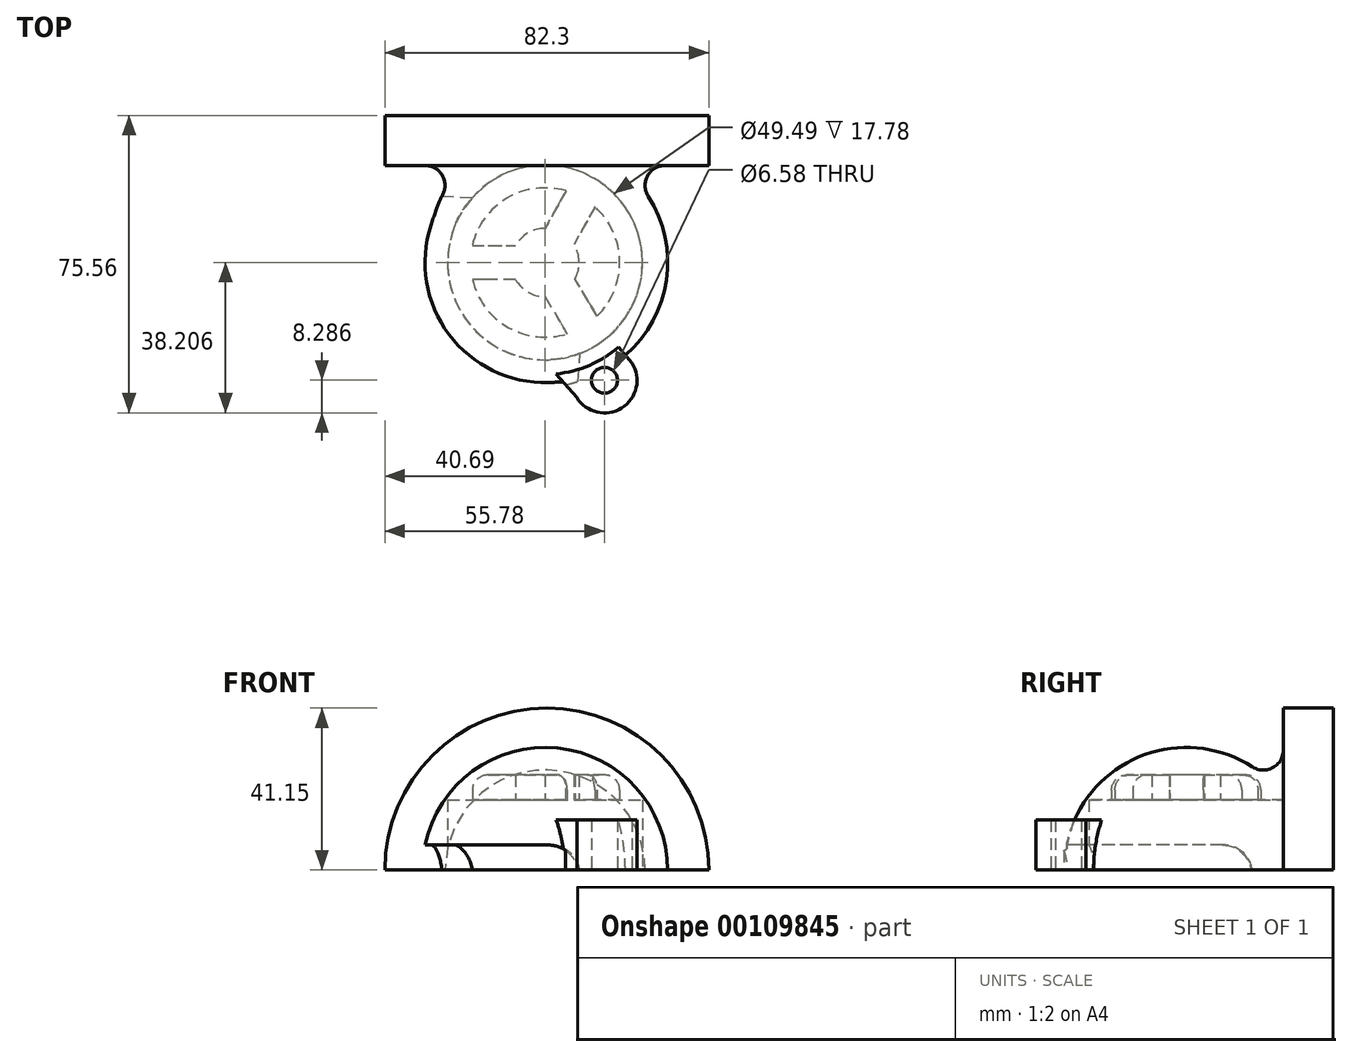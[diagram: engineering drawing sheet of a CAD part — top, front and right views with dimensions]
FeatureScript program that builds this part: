
annotation { "Feature Type Name" : "Feature", "Feature Type Description" : "" }
export const myFeature = defineFeature(function(context is Context, id is Id, definition is map)
    precondition{}
    {
        {
            var Q0;
            Q0=qCreatedBy(makeId("Front.planeOp"),FACE);
            var sketch = newSketch(context, id + "F0", { "sketchPlane" : qUnion([Q0])});
            skArc(sketch, "E0", {"start": v(41.6, 0) * mm, "mid": v(0.46, 41.15) * mm, "end": v(-40.7, 0) * mm});
            skLineSegment(sketch, "E1", {"start": v(-40.7, 0) * mm, "end": v(41.6, 0) * mm});
            skSolve(sketch);
        }
        {
            var Q0;
            Q0 = qSketchRegion(id + "F0", true);
            extrude(context, id + "F1", {"entities" : qUnion([Q0]), "oppositeDirection" : true, "depth" : 12.7 * mm});
        }
        {
            var Q0;
            Q0=qCreatedBy(makeId("Top.planeOp"),FACE);
            var sketch = newSketch(context, id + "F2", { "sketchPlane" : qUnion([Q0])});
            skCircle(sketch, "E2", {"center": v(0, -24.65) * mm, "radius": 31.14 * mm});
            skLineSegment(sketch, "E3", {"start": v(0, -55.8) * mm, "end": v(0, 0) * mm});
            skLineSegment(sketch, "E4", {"start": v(0, -67.73) * mm, "end": v(0, 47.75) * mm, "construction": true});
            skLineSegment(sketch, "E5", {"start": v(0, -55.8) * mm, "end": v(0, 6.5) * mm});
            skSolve(sketch);
        }
        {
            var Q0;
            {var subQ0=sQuery(id+"F2.wireOp",EDGE,"E5");var subQ4=makeQuery(id+"F2.imprint","IMPRINT",VERTEX,{"derivedFrom":subQ0});Q0=makeQuery(id+"F2.imprint","IMPRINT",FACE,{"disambiguationData":[TD([[makeQuery(id+"F2.imprint","IMPRINT",EDGE,{"disambiguationData":[TD([[subQ4,1.0]])],"derivedFrom":subQ0}),-1.0]])]});}
            var Q1;
            Q1=sQuery(id+"F2.wireOp",EDGE,"E4");
            revolve(context, id + "F3", {"operationType" : NewBodyOperationType.ADD, "entities" : qUnion([Q0]), "axis" : qUnion([Q1]), "revolveType" : RevolveType.ONE_DIRECTION, "oppositeDirection" : true, "angle" : 180 * degree});
        }
        {
            var Q0;
            Q0=makeQuery(id+"F3.boolean.opBoolean","INTERSECT",EDGE,{"derivedFrom":[makeQuery(id+"F1.opExtrude","CAP_FACE",FACE,{"disambiguationData":[OSD([sQuery(id+"F0.wireOp",EDGE,"E0"),sQuery(id+"F0.wireOp",EDGE,"E1")])],"isStart":true}),makeQuery(id+"F3.opRevolve","SWEPT_FACE",FACE,{"disambiguationData":[OSD([sQuery(id+"F2.wireOp",EDGE,"E2")])]})]});
            fillet(context, id + "F4", {"entities" : qUnion([Q0]), "radius" : 5.08 * mm, "tangentPropagation" : true, "allowEdgeOverflow" : false});
        }
        {
            var Q0;
            Q0=makeQuery(id+"F3.boolean.opBoolean","MERGE",FACE,{"derivedFrom":[makeQuery(id+"F1.opExtrude","SWEPT_FACE",FACE,{"disambiguationData":[OSD([sQuery(id+"F0.wireOp",EDGE,"E1")])]}),makeQuery(id+"F3.opRevolve","CAP_FACE",FACE,{"disambiguationData":[OSD([sQuery(id+"F2.wireOp",EDGE,"E2"),sQuery(id+"F2.wireOp",EDGE,"E5")])],"isStart":true})]});
            var sketch = newSketch(context, id + "F5", { "sketchPlane" : qUnion([Q0])});
            skCircle(sketch, "E6", {"center": v(0, 24.65) * mm, "radius": 24.75 * mm});
            skSolve(sketch);
        }
        {
            var Q0;
            Q0 = qSketchRegion(id + "F5", true);
            extrude(context, id + "F6", {"entities" : qUnion([Q0]), "operationType" : NewBodyOperationType.REMOVE, "oppositeDirection" : true, "depth" : 17.78 * mm});
        }
        {
            var Q0;
            Q0=makeQuery(id+"F6.boolean.opBoolean","COPY",FACE,{"derivedFrom":makeQuery(id+"F6.opExtrude","CAP_FACE",FACE,{"disambiguationData":[OSD([sQuery(id+"F5.wireOp",EDGE,"E6")])],"isStart":false})});
            var sketch = newSketch(context, id + "F7", { "sketchPlane" : qUnion([Q0])});
            skCircle(sketch, "E7", {"center": v(0, 24.65) * mm, "radius": 18.97 * mm});
            skCircle(sketch, "E8", {"center": v(0, 24.65) * mm, "radius": 8.68 * mm});
            skLineSegment(sketch, "E9", {"start": v(-7.53, 28.97) * mm, "end": v(-18.48, 28.97) * mm});
            skLineSegment(sketch, "E10", {"start": v(-18.48, 28.97) * mm, "end": v(-18.48, 20.34) * mm});
            skLineSegment(sketch, "E11", {"start": v(-18.48, 20.34) * mm, "end": v(-7.53, 20.34) * mm});
            skLineSegment(sketch, "E12", {"start": v(-7.53, 28.97) * mm, "end": v(-7.53, 20.34) * mm});
            skLineSegment(sketch, "E13", {"start": v(0, 33.33) * mm, "end": v(5.61, 42.78) * mm});
            skLineSegment(sketch, "E14", {"start": v(5.33, 6.44) * mm, "end": v(0, 15.98) * mm});
            skLineSegment(sketch, "E15", {"start": v(5.22, 6.41) * mm, "end": v(12.67, 10.53) * mm});
            skLineSegment(sketch, "E16", {"start": v(12.67, 10.53) * mm, "end": v(7.35, 20.04) * mm});
            skLineSegment(sketch, "E17", {"start": v(7.35, 20.04) * mm, "end": v(0, 15.98) * mm});
            skLineSegment(sketch, "E18", {"start": v(5.61, 42.78) * mm, "end": v(13.23, 38.25) * mm});
            skLineSegment(sketch, "E19", {"start": v(13.23, 38.25) * mm, "end": v(7.62, 28.8) * mm});
            skLineSegment(sketch, "E20", {"start": v(7.62, 28.8) * mm, "end": v(0, 33.33) * mm});
            skSolve(sketch);
        }
        {
            var Q0;
            {var subQ0=sQuery(id+"F7.wireOp",EDGE,"E9");Q0=makeQuery(id+"F7.imprint","IMPRINT",FACE,{"disambiguationData":[TD([[makeQuery(id+"F7.imprint","IMPRINT",EDGE,{"derivedFrom":subQ0}),-1.0]])]});}
            var Q1;
            {var subQ0=sQuery(id+"F7.wireOp",EDGE,"E16");Q1=makeQuery(id+"F7.imprint","IMPRINT",FACE,{"disambiguationData":[TD([[makeQuery(id+"F7.imprint","IMPRINT",EDGE,{"derivedFrom":subQ0}),-1.0]])]});}
            var Q2;
            {var subQ0=sQuery(id+"F7.wireOp",EDGE,"E11");Q2=makeQuery(id+"F7.imprint","IMPRINT",FACE,{"disambiguationData":[TD([[makeQuery(id+"F7.imprint","IMPRINT",EDGE,{"derivedFrom":subQ0}),-1.0]])]});}
            extrude(context, id + "F8", {"entities" : qUnion([Q0, Q1, Q2]), "operationType" : NewBodyOperationType.REMOVE, "oppositeDirection" : true, "depth" : 6.35 * mm});
        }
        {
            var Q0;
            Q0=qCreatedBy(makeId("Top.planeOp"),FACE);
            var sketch = newSketch(context, id + "F9", { "sketchPlane" : qUnion([Q0])});
            skLineSegment(sketch, "E21", {"start": v(16.9, -44.18) * mm, "end": v(2.16, -52.16) * mm});
            skArc(sketch, "E22", {"start": v(8.07, -58.97) * mm, "mid": v(19.49, -61.6) * mm, "end": v(22.11, -50.18) * mm});
            skLineSegment(sketch, "E23", {"start": v(22.11, -50.18) * mm, "end": v(16.9, -44.18) * mm});
            skLineSegment(sketch, "E24", {"start": v(8.07, -58.97) * mm, "end": v(2.16, -52.16) * mm});
            skSolve(sketch);
        }
        {
            var Q0;
            Q0 = qSketchRegion(id + "F9", true);
            extrude(context, id + "F10", {"entities" : qUnion([Q0]), "operationType" : NewBodyOperationType.ADD, "depth" : 12.7 * mm});
        }
        {
            var Q0;
            Q0=makeQuery(id+"F10.boolean.opBoolean","MERGE",FACE,{"derivedFrom":[makeQuery(id+"F3.boolean.opBoolean","MERGE",FACE,{"derivedFrom":[makeQuery(id+"F1.opExtrude","SWEPT_FACE",FACE,{"disambiguationData":[OSD([sQuery(id+"F0.wireOp",EDGE,"E1")])]}),makeQuery(id+"F3.opRevolve","CAP_FACE",FACE,{"disambiguationData":[OSD([sQuery(id+"F2.wireOp",EDGE,"E2"),sQuery(id+"F2.wireOp",EDGE,"E5")])],"isStart":true})]}),makeQuery(id+"F10.opExtrude","CAP_FACE",FACE,{"disambiguationData":[OSD([sQuery(id+"F9.wireOp",EDGE,"E21"),sQuery(id+"F9.wireOp",EDGE,"E22"),sQuery(id+"F9.wireOp",EDGE,"E23"),sQuery(id+"F9.wireOp",EDGE,"E24")])],"isStart":true})]});
            var sketch = newSketch(context, id + "F11", { "sketchPlane" : qUnion([Q0])});
            skCircle(sketch, "E25", {"center": v(15.09, 54.57) * mm, "radius": 3.29 * mm});
            skSolve(sketch);
        }
        {
            var Q0;
            Q0 = qSketchRegion(id + "F11", true);
            extrude(context, id + "F12", {"entities" : qUnion([Q0]), "operationType" : NewBodyOperationType.REMOVE, "oppositeDirection" : true, "depth" : 50.8 * mm});
        }
        {
            var Q0;
            Q0=qCreatedBy(makeId("Top.planeOp"),FACE);
            var sketch = newSketch(context, id + "F13", { "sketchPlane" : qUnion([Q0])});
            skArc(sketch, "E26", {"start": v(-26.4, -7.8) * mm, "mid": v(-26.22, -44.06) * mm, "end": v(8.4, -54.85) * mm});
            skArc(sketch, "E27", {"start": v(-16.68, -8.24) * mm, "mid": v(-20.25, -38.17) * mm, "end": v(9.02, -45.34) * mm});
            skLineSegment(sketch, "E28", {"start": v(-26.4, -7.8) * mm, "end": v(-16.68, -8.24) * mm});
            skLineSegment(sketch, "E29", {"start": v(8.4, -54.85) * mm, "end": v(9.02, -45.34) * mm});
            skSolve(sketch);
        }
        {
            var Q0;
            Q0 = qSketchRegion(id + "F13", true);
            extrude(context, id + "F14", {"entities" : qUnion([Q0]), "operationType" : NewBodyOperationType.REMOVE, "depth" : 6.35 * mm});
        }
        {
            var Q0;
            Q0=makeQuery(id+"F14.boolean.opBoolean","COPY",EDGE,{"derivedFrom":makeQuery(id+"F14.opExtrude","CAP_EDGE",EDGE,{"disambiguationData":[OSD([sQuery(id+"F13.wireOp",EDGE,"E29")])],"isStart":false})});
            var Q1;
            Q1=makeQuery(id+"F14.boolean.opBoolean","COPY",EDGE,{"derivedFrom":makeQuery(id+"F14.opExtrude","CAP_EDGE",EDGE,{"disambiguationData":[OSD([sQuery(id+"F13.wireOp",EDGE,"E28")])],"isStart":false})});
            fillet(context, id + "F15", {"entities" : qUnion([Q0, Q1]), "radius" : 7.62 * mm, "tangentPropagation" : true, "allowEdgeOverflow" : false});
        }
        {
            var Q0;
            {var subQ0=sQuery(id+"F7.wireOp",EDGE,"E7");Q0=makeQuery(id+"F8.boolean.opBoolean","COPY",EDGE,{"derivedFrom":makeQuery(id+"F8.opExtrude","CAP_EDGE",EDGE,{"disambiguationData":[OSD([subQ0]),TDD([makeQuery(id+"F7.imprint","IMPRINT",EDGE,{"disambiguationData":[TD([[makeQuery(id+"F7.imprint","INTERSECT",VERTEX,{"derivedFrom":[subQ0,sQuery(id+"F7.wireOp",EDGE,"E9"),sQuery(id+"F7.wireOp",EDGE,"E10")]}),1.0]])],"derivedFrom":subQ0})])],"isStart":false})});}
            var Q1;
            {var subQ0=sQuery(id+"F7.wireOp",EDGE,"E7");Q1=makeQuery(id+"F8.boolean.opBoolean","COPY",EDGE,{"derivedFrom":makeQuery(id+"F8.opExtrude","CAP_EDGE",EDGE,{"disambiguationData":[OSD([subQ0]),TDD([makeQuery(id+"F7.imprint","IMPRINT",EDGE,{"disambiguationData":[TD([[makeQuery(id+"F7.imprint","INTERSECT",VERTEX,{"derivedFrom":[subQ0,sQuery(id+"F7.wireOp",EDGE,"E15"),sQuery(id+"F7.wireOp",EDGE,"E16")]}),-1.0]])],"derivedFrom":subQ0})])],"isStart":false})});}
            var Q2;
            {var subQ0=sQuery(id+"F7.wireOp",EDGE,"E7");Q2=makeQuery(id+"F8.boolean.opBoolean","COPY",EDGE,{"derivedFrom":makeQuery(id+"F8.opExtrude","CAP_EDGE",EDGE,{"disambiguationData":[OSD([subQ0]),TDD([makeQuery(id+"F7.imprint","IMPRINT",EDGE,{"disambiguationData":[TD([[makeQuery(id+"F7.imprint","INTERSECT",VERTEX,{"derivedFrom":[subQ0,sQuery(id+"F7.wireOp",EDGE,"E15")]}),1.0]])],"derivedFrom":subQ0})])],"isStart":false})});}
            fillet(context, id + "F16", {"entities" : qUnion([Q0, Q1, Q2]), "radius" : 3.8 * mm, "tangentPropagation" : true, "allowEdgeOverflow" : false});
        }
    });
